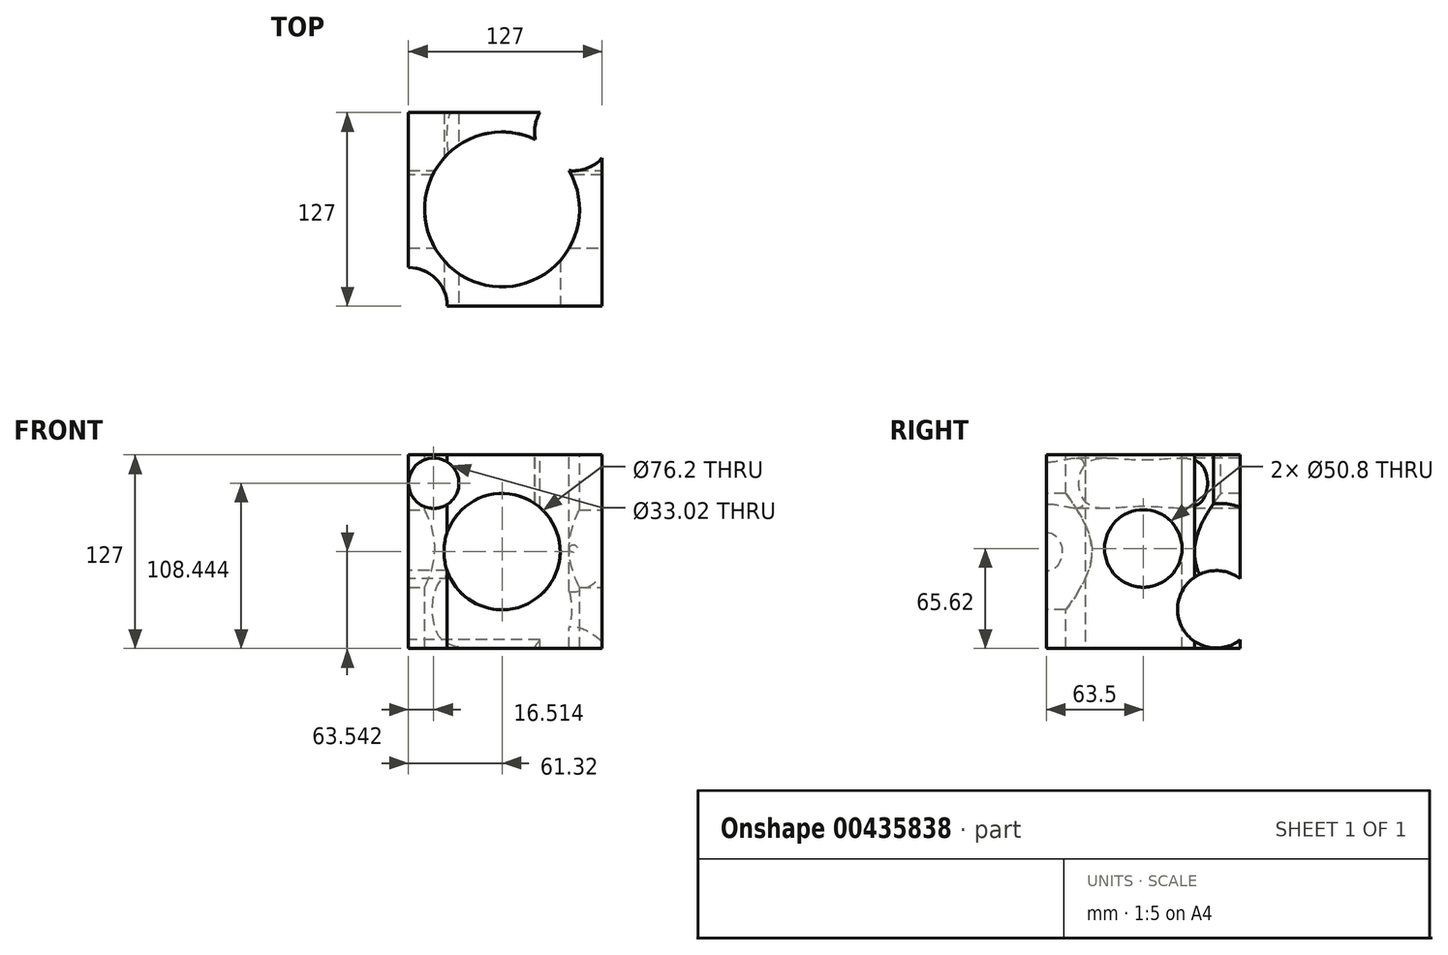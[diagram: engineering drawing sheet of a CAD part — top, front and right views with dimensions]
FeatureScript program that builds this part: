
annotation { "Feature Type Name" : "Feature", "Feature Type Description" : "" }
export const myFeature = defineFeature(function(context is Context, id is Id, definition is map)
    precondition{}
    {
        {
            var Q0;
            Q0=qCreatedBy(makeId("Front.planeOp"),FACE);
            var sketch = newSketch(context, id + "F0", { "sketchPlane" : qUnion([Q0])});
            skLineSegment(sketch, "E0.bottom", {"start": v(-61.32, 61.38) * mm, "end": v(65.68, 61.38) * mm});
            skLineSegment(sketch, "E0.top", {"start": v(-61.32, -65.62) * mm, "end": v(65.68, -65.62) * mm});
            skLineSegment(sketch, "E0.left", {"start": v(-61.32, 61.38) * mm, "end": v(-61.32, -65.62) * mm});
            skLineSegment(sketch, "E0.right", {"start": v(65.68, 61.38) * mm, "end": v(65.68, -65.62) * mm});
            skSolve(sketch);
        }
        {
            var Q0;
            Q0 = qSketchRegion(id + "F0", true);
            extrude(context, id + "F1", {"entities" : qUnion([Q0]), "depth" : 127 * mm});
        }
        {
            var Q0;
            Q0=makeQuery(id+"F1.opExtrude","SWEPT_FACE",FACE,{"disambiguationData":[OSD([sQuery(id+"F0.wireOp",EDGE,"E0.bottom")])]});
            var sketch = newSketch(context, id + "F2", { "sketchPlane" : qUnion([Q0])});
            skPoint(sketch, "E1", {"position": v(0, -63.5) * mm});
            skSolve(sketch);
        }
        {
            var Q0;
            Q0=sQuery(id+"F2.wireOp",VERTEX,"E1");
            var Q1;
            Q1=makeQuery(id+"F1.opExtrude","SWEPT_BODY",BODY,{"disambiguationData":[OSD([sQuery(id+"F0.wireOp",EDGE,"E0.bottom"),sQuery(id+"F0.wireOp",EDGE,"E0.top"),sQuery(id+"F0.wireOp",EDGE,"E0.left"),sQuery(id+"F0.wireOp",EDGE,"E0.right")])]});
            hole(context, id + "F3", {"style" : HoleStyle.SIMPLE, "endStyle" : HoleEndStyle.THROUGH, "holeDiameter" : 101.6 * mm, "isTappedThrough" : true, "tappedDepth" : 12.7 * mm, "tapClearance" : 3, "locations" : qUnion([Q0]), "scope" : qUnion([Q1])});
        }
        {
            var Q0;
            Q0=makeQuery(id+"F1.opExtrude","CAP_FACE",FACE,{"disambiguationData":[OSD([sQuery(id+"F0.wireOp",EDGE,"E0.bottom"),sQuery(id+"F0.wireOp",EDGE,"E0.top"),sQuery(id+"F0.wireOp",EDGE,"E0.left"),sQuery(id+"F0.wireOp",EDGE,"E0.right")])],"isStart":false});
            var sketch = newSketch(context, id + "F4", { "sketchPlane" : qUnion([Q0])});
            skPoint(sketch, "E2", {"position": v(0, -2.08) * mm});
            skSolve(sketch);
        }
        {
            var Q0;
            Q0=sQuery(id+"F4.wireOp",VERTEX,"E2");
            var Q1;
            Q1=makeQuery(id+"F1.opExtrude","SWEPT_BODY",BODY,{"disambiguationData":[OSD([sQuery(id+"F0.wireOp",EDGE,"E0.bottom"),sQuery(id+"F0.wireOp",EDGE,"E0.top"),sQuery(id+"F0.wireOp",EDGE,"E0.left"),sQuery(id+"F0.wireOp",EDGE,"E0.right")])]});
            hole(context, id + "F5", {"style" : HoleStyle.SIMPLE, "endStyle" : HoleEndStyle.THROUGH, "holeDiameter" : 76.2 * mm, "isTappedThrough" : true, "tappedDepth" : 12.7 * mm, "tapClearance" : 3, "locations" : qUnion([Q0]), "scope" : qUnion([Q1])});
        }
        {
            var Q0;
            Q0=makeQuery(id+"F1.opExtrude","SWEPT_FACE",FACE,{"disambiguationData":[OSD([sQuery(id+"F0.wireOp",EDGE,"E0.right")])]});
            var sketch = newSketch(context, id + "F6", { "sketchPlane" : qUnion([Q0])});
            skPoint(sketch, "E3", {"position": v(-63.5, 0) * mm});
            skSolve(sketch);
        }
        {
            var Q0;
            Q0=sQuery(id+"F6.wireOp",VERTEX,"E3");
            var Q1;
            Q1=makeQuery(id+"F1.opExtrude","SWEPT_BODY",BODY,{"disambiguationData":[OSD([sQuery(id+"F0.wireOp",EDGE,"E0.bottom"),sQuery(id+"F0.wireOp",EDGE,"E0.top"),sQuery(id+"F0.wireOp",EDGE,"E0.left"),sQuery(id+"F0.wireOp",EDGE,"E0.right")])]});
            hole(context, id + "F7", {"style" : HoleStyle.SIMPLE, "endStyle" : HoleEndStyle.THROUGH, "holeDiameter" : 50.8 * mm, "isTappedThrough" : true, "tappedDepth" : 12.7 * mm, "tapClearance" : 3, "locations" : qUnion([Q0]), "scope" : qUnion([Q1])});
        }
        {
            var Q0;
            Q0=makeQuery(id+"F1.opExtrude","SWEPT_FACE",FACE,{"disambiguationData":[OSD([sQuery(id+"F0.wireOp",EDGE,"E0.left")])]});
            var sketch = newSketch(context, id + "F8", { "sketchPlane" : qUnion([Q0])});
            skPoint(sketch, "E4", {"position": v(15.61, -39.91) * mm});
            skSolve(sketch);
        }
        {
            var Q0;
            Q0=sQuery(id+"F8.wireOp",VERTEX,"E4");
            var Q1;
            Q1=makeQuery(id+"F1.opExtrude","SWEPT_BODY",BODY,{"disambiguationData":[OSD([sQuery(id+"F0.wireOp",EDGE,"E0.bottom"),sQuery(id+"F0.wireOp",EDGE,"E0.top"),sQuery(id+"F0.wireOp",EDGE,"E0.left"),sQuery(id+"F0.wireOp",EDGE,"E0.right")])]});
            hole(context, id + "F9", {"style" : HoleStyle.SIMPLE, "endStyle" : HoleEndStyle.THROUGH, "holeDiameter" : 50.8 * mm, "isTappedThrough" : true, "tappedDepth" : 12.7 * mm, "tapClearance" : 3, "locations" : qUnion([Q0]), "scope" : qUnion([Q1])});
        }
        {
            var Q0;
            Q0=makeQuery(id+"F1.opExtrude","SWEPT_FACE",FACE,{"disambiguationData":[OSD([sQuery(id+"F0.wireOp",EDGE,"E0.bottom")])]});
            var sketch = newSketch(context, id + "F10", { "sketchPlane" : qUnion([Q0])});
            skPoint(sketch, "E5", {"position": v(46.74, -12.83) * mm});
            skSolve(sketch);
        }
        {
            var Q0;
            Q0=sQuery(id+"F10.wireOp",VERTEX,"E5");
            var Q1;
            Q1=makeQuery(id+"F1.opExtrude","SWEPT_BODY",BODY,{"disambiguationData":[OSD([sQuery(id+"F0.wireOp",EDGE,"E0.bottom"),sQuery(id+"F0.wireOp",EDGE,"E0.top"),sQuery(id+"F0.wireOp",EDGE,"E0.left"),sQuery(id+"F0.wireOp",EDGE,"E0.right")])]});
            hole(context, id + "F11", {"style" : HoleStyle.SIMPLE, "endStyle" : HoleEndStyle.THROUGH, "holeDiameter" : 50.8 * mm, "isTappedThrough" : true, "tappedDepth" : 12.7 * mm, "tapClearance" : 3, "locations" : qUnion([Q0]), "scope" : qUnion([Q1])});
        }
        {
            var Q0;
            Q0=makeQuery(id+"F1.opExtrude","CAP_FACE",FACE,{"disambiguationData":[OSD([sQuery(id+"F0.wireOp",EDGE,"E0.bottom"),sQuery(id+"F0.wireOp",EDGE,"E0.top"),sQuery(id+"F0.wireOp",EDGE,"E0.left"),sQuery(id+"F0.wireOp",EDGE,"E0.right")])],"isStart":false});
            var sketch = newSketch(context, id + "F12", { "sketchPlane" : qUnion([Q0])});
            skPoint(sketch, "E6", {"position": v(-44.8, 42.82) * mm});
            skSolve(sketch);
        }
        {
            var Q0;
            Q0=sQuery(id+"F12.wireOp",VERTEX,"E6");
            var Q1;
            Q1=makeQuery(id+"F1.opExtrude","SWEPT_BODY",BODY,{"disambiguationData":[OSD([sQuery(id+"F0.wireOp",EDGE,"E0.bottom"),sQuery(id+"F0.wireOp",EDGE,"E0.top"),sQuery(id+"F0.wireOp",EDGE,"E0.left"),sQuery(id+"F0.wireOp",EDGE,"E0.right")])]});
            hole(context, id + "F13", {"style" : HoleStyle.SIMPLE, "endStyle" : HoleEndStyle.THROUGH, "holeDiameter" : 33.02 * mm, "isTappedThrough" : true, "tappedDepth" : 12.7 * mm, "tapClearance" : 3, "locations" : qUnion([Q0]), "scope" : qUnion([Q1])});
        }
        {
            var Q0;
            Q0=makeQuery(id+"F1.opExtrude","SWEPT_FACE",FACE,{"disambiguationData":[OSD([sQuery(id+"F0.wireOp",EDGE,"E0.top")])]});
            var sketch = newSketch(context, id + "F14", { "sketchPlane" : qUnion([Q0])});
            skPoint(sketch, "E7", {"position": v(-61.32, 127) * mm});
            skSolve(sketch);
        }
        {
            var Q0;
            Q0=sQuery(id+"F14.wireOp",VERTEX,"E7");
            var Q1;
            Q1=makeQuery(id+"F1.opExtrude","SWEPT_BODY",BODY,{"disambiguationData":[OSD([sQuery(id+"F0.wireOp",EDGE,"E0.bottom"),sQuery(id+"F0.wireOp",EDGE,"E0.top"),sQuery(id+"F0.wireOp",EDGE,"E0.left"),sQuery(id+"F0.wireOp",EDGE,"E0.right")])]});
            hole(context, id + "F15", {"style" : HoleStyle.SIMPLE, "endStyle" : HoleEndStyle.THROUGH, "holeDiameter" : 50.8 * mm, "isTappedThrough" : true, "tappedDepth" : 12.7 * mm, "tapClearance" : 3, "locations" : qUnion([Q0]), "scope" : qUnion([Q1])});
        }
    });
